# Revit family: Bathtub-American_Standard-Colony-018X_Series
name_source: partatom
category: Plumbing Fixtures
units: mm (PartAtom-declared; Revit-internal decimal feet)

## family parameters
Always vertical = No
Cut with Voids When Loaded = No
OmniClass Number = 23.45.05.14.21.11
OmniClass Title = Bath/Shower Units
Part Type = Normal
Room Calculation Point = No
Round Connector Dimension = Use Radius
Shared = Yes
Work Plane-Based = Yes

## types (8) — shared parameters
ADA Compliant = Yes
Assembly Code = D2010510
CW Connection = No
CWFU = 1.5
Default Elevation = 0"
HW Connection = No
HWFU = 1.5
Height = 17 7/16"
IAPMO Compliance = Compliance Certifications - Meets or Exceeds the Following Specifications:  ASME A112.19.4M for Enamelled Steel Fixtures and ASTM F-462 for Slip-resistant Bathing Facilities and  CAN/CSA B45 Series
Installation Type = Floor Mount
Length = 30"
Manufacturer = American Standard
OverfLow Extrusion Start = 0"
Product Documentation Link = https://americanstandard.box.com
Product Page URL = https://www.americanstandard.ca
Revised Date = 12/07/2018
URL = https://www.americanstandard.ca
Vent Connection = No
WFU = 2
Waste Connection = Yes
Waste Connection Diameter = 1 1/2"
Waste Connection Radius = 3/4"
Width = 60"

## per-type parameters (varying)
| type | Description | Finish | Material | Outlet Location | OverflowExtrusion Ends | Slip Resistant Surface | Sound Deadening |
| 0184000.020 | Colony 5x30 Inch Integral Apron Bathtub Above Floor Rough with Left-hand Outlet | Enamelled Steel-American Standard-020-White | Enamelled Steel-American Standard-020-White | 8 1/2" | -30" | No | No |
| 0182000.020 | Colony 5x30 Inch Integral Apron Bathtub Above Floor Rough with Right-hand Outlet | Enamelled Steel-American Standard-020-White | Enamelled Steel-American Standard-020-White | 50" | 30" | No | No |
| 0182000.021 | Colony 5x30 Inch Integral Apron Bathtub Above Floor Rough with Right-hand Outlet | Enamelled Steel-American Standard-021-Bone | Enamelled Steel-American Standard-021-Bone | 50" | 30" | No | No |
| 0182331.020 | Colony 5x30 Inch Integral Apron Bathtub Above Floor Rough Right-hand Outlet with Slip Resistant Foor and Sound Deadening | Enamelled Steel-American Standard-020-White | Enamelled Steel-American Standard-020-White | 50" | 30" | Yes | Yes |
| 0182S00.020 | Colony 5x30 Inch Integral Apron Bathtub Above Floor Rough Right-hand Outlet with Slip Resistant Foor | Enamelled Steel-American Standard-020-White | Enamelled Steel-American Standard-020-White | 50" | 30" | Yes | No |
| 0184000.021 | Colony 5x30 Inch Integral Apron Bathtub Above Floor Rough with Left-hand Outlet | Enamelled Steel-American Standard-021-Bone | Enamelled Steel-American Standard-021-Bone | 8 1/2" | -30" | No | No |
| 0184331.020 | Colony 5x30 Inch Integral Apron Bathtub Above Floor Rough Left-hand Outlet with Slip Resistant Foor and Sound Deadening | Enamelled Steel-American Standard-020-White | Enamelled Steel-American Standard-020-White | 8 1/2" | -30" | Yes | Yes |
| 0184S00.020 | Colony 5x30 Inch Integral Apron Bathtub Above Floor Rough Left-hand Outlet with Slip Resistant Foor | Enamelled Steel-American Standard-020-White | Enamelled Steel-American Standard-020-White | 8 1/2" | -30" | Yes | No |

note: column(s) folded — value = type name in every type: Model

## geometry (parser evidence)
native form markers: Extrusion x2, Sweep x2
no freeform markers — native parametric forms only
